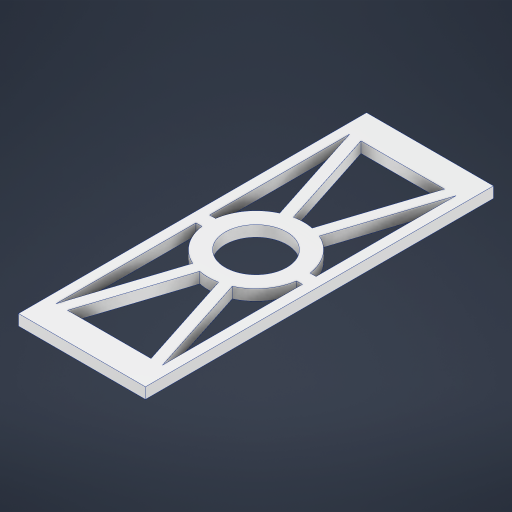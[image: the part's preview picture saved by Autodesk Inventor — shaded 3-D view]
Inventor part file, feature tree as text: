
AUTODESK INVENTOR PART (.ipt)
format: ipt  version: 2024 (Build 280153000, 153)  size: 304,128 bytes
history: native  units: mm
features: extrude x5, sketch x5, projected_geometry x1
ambient origin geometry x8: Origin, YZ Plane, XZ Plane, XY Plane, X Axis, Y Axis, Z Axis, Center Point
bodies: Solid1 (feature_tree)
feature tree (11):
  extrude  "Extrusion1"  Depth=186.0mm
  extrude  "Extrusion2"  Depth=16.0mm TaperAngle=0.0deg
  extrude  "Extrusion3"  Depth=25.0mm
  extrude  "Extrusion4"  Depth=50.0mm
  extrude  "Extrusion5"  Depth=15.0mm
  sketch  "Sketch1"  dims[d0=542.0mm d1=186.0mm]
  sketch  "Sketch2"  dims[d2=90.0mm d3=16.0mm d4=0.0mm]
  sketch  "Sketch3"  dims[d5=6.0mm d6=25.0mm]
  projected_geometry  "Projected Loop1"
  sketch  "Sketch4"  dims[d7=25.0mm d8=50.0mm]
  sketch  "Sketch5"  dims[d9=15.0mm d10=15.0mm d11=50.0mm d12=20.0mm d13=0.0mm d14=25.0mm d15=15.0mm d16=10.0mm d17=10.0mm d18=8.0mm d19=8.0mm d20=8.0mm d21=8.0mm d22=20.0mm d23=0.0mm d24=16.0mm d25=0.0mm d26=40.0mm d27=40.0mm d28=100.0mm d29=0.0mm]
